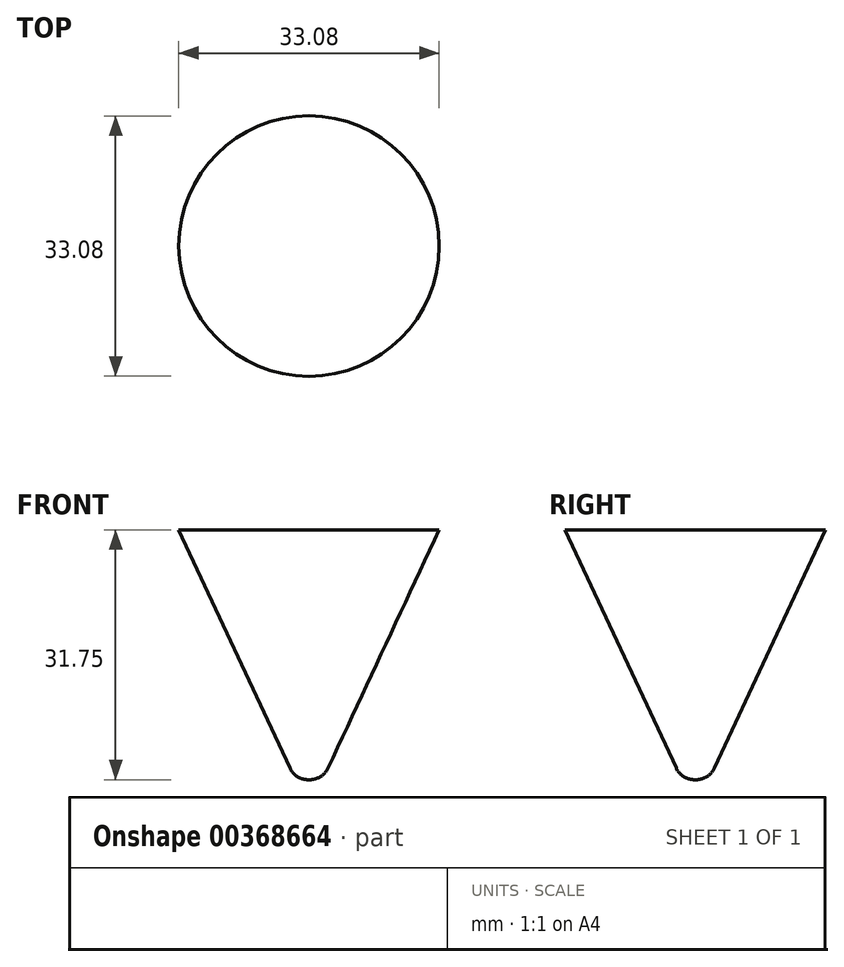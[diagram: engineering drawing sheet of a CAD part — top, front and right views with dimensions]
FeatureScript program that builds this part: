
annotation { "Feature Type Name" : "Feature", "Feature Type Description" : "" }
export const myFeature = defineFeature(function(context is Context, id is Id, definition is map)
    precondition{}
    {
        {
            var Q0;
            Q0=qCreatedBy(makeId("Top.planeOp"),FACE);
            cPlane(context, id + "F0", {"entities" : qUnion([Q0]), "cplaneType" : CPlaneType.OFFSET, "offset" : 25.4 * mm, "oppositeDirection" : true, "width" : 152.4 * mm, "height" : 152.4 * mm});
        }
        {
            var Q0;
            Q0=qCreatedBy(id+"F0.planeOp",FACE);
            var sketch = newSketch(context, id + "F1", { "sketchPlane" : qUnion([Q0])});
            skCircle(sketch, "E0", {"center": v(0, 0) * mm, "radius": 4.7 * mm});
            skSolve(sketch);
        }
        {
            var Q0;
            Q0 = qSketchRegion(id + "F1", true);
            extrude(context, id + "F2", {"entities" : qUnion([Q0]), "oppositeDirection" : true, "depth" : 6.35 * mm, "hasDraft" : true, "draftAngle" : 25 * degree, "draftPullDirection" : true});
        }
        {
            var Q0;
            Q0=makeQuery(id+"F2.opExtrude","CAP_EDGE",EDGE,{"disambiguationData":[OSD([sQuery(id+"F1.wireOp",EDGE,"E0")])],"isStart":false});
            fillet(context, id + "F3", {"entities" : qUnion([Q0]), "radius" : 2.54 * mm, "tangentPropagation" : true, "allowEdgeOverflow" : false});
        }
        {
            var Q0;
            Q0=qCreatedBy(id+"F0.planeOp",FACE);
            var sketch = newSketch(context, id + "F4", { "sketchPlane" : qUnion([Q0])});
            skCircle(sketch, "E1", {"center": v(0, 0) * mm, "radius": 4.7 * mm});
            skSolve(sketch);
        }
        {
            var Q0;
            Q0 = qSketchRegion(id + "F4", true);
            extrude(context, id + "F5", {"entities" : qUnion([Q0]), "operationType" : NewBodyOperationType.ADD, "depth" : 25.4 * mm, "hasDraft" : true, "draftAngle" : 25 * degree});
        }
    });
